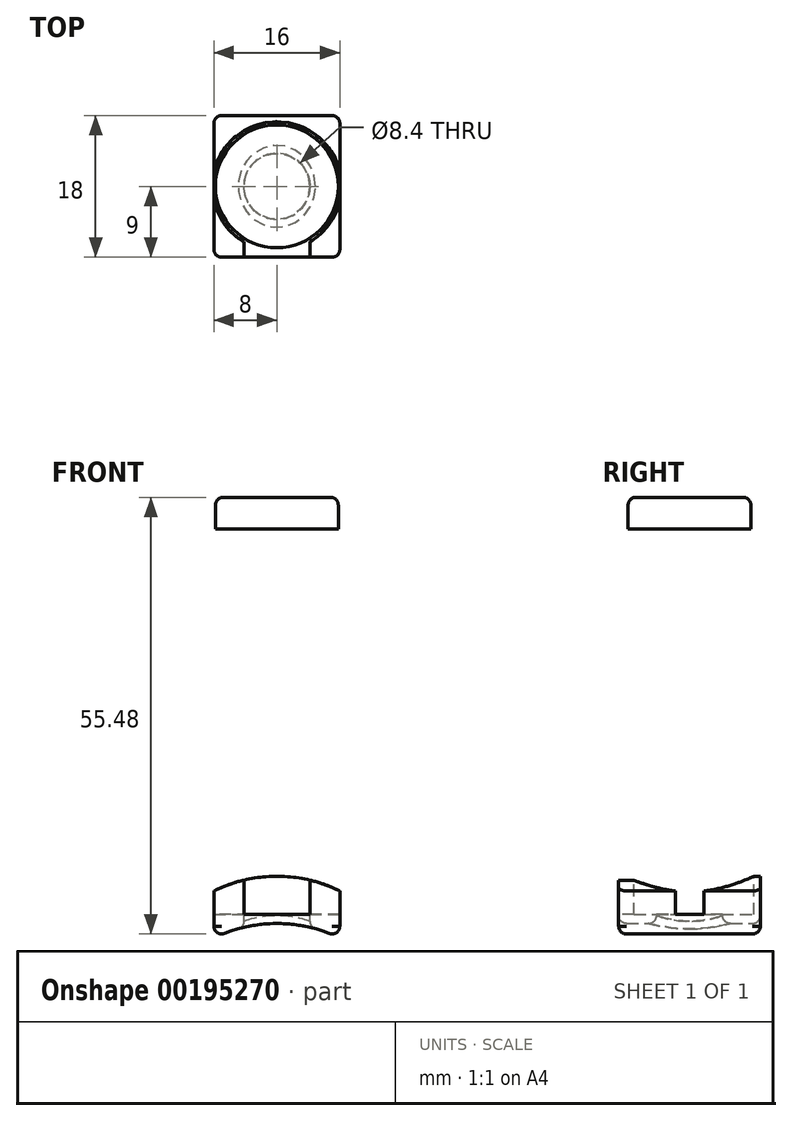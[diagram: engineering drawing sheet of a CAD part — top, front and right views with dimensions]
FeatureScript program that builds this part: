
annotation { "Feature Type Name" : "Feature", "Feature Type Description" : "" }
export const myFeature = defineFeature(function(context is Context, id is Id, definition is map)
    precondition{}
    {
        {
            var Q0;
            Q0=qCreatedBy(makeId("Front.planeOp"),FACE);
            var sketch = newSketch(context, id + "F0", { "sketchPlane" : qUnion([Q0])});
            skLineSegment(sketch, "E0.left", {"start": v(8, 2.02) * mm, "end": v(8, -2.02) * mm});
            skLineSegment(sketch, "E0.right", {"start": v(-8, 2.02) * mm, "end": v(-8, -2.02) * mm});
            skPoint(sketch, "E0.middle", {"position": v(0, 0) * mm});
            skArc(sketch, "E1", {"start": v(8, -2.02) * mm, "mid": v(0, -0.14) * mm, "end": v(-8, -2.02) * mm});
            skArc(sketch, "E2", {"start": v(8, 3.98) * mm, "mid": v(0, 5.86) * mm, "end": v(-8, 3.98) * mm});
            skLineSegment(sketch, "E3", {"start": v(-8, 2.02) * mm, "end": v(-8, 3.98) * mm});
            skLineSegment(sketch, "E4", {"start": v(8, 2.02) * mm, "end": v(8, 3.98) * mm});
            skSolve(sketch);
        }
        {
            var Q0;
            Q0=qSketchRegion(id+"F0",true);
            extrude(context, id + "F1", {"entities" : qUnion([Q0]), "endBound" : BoundingType.SYMMETRIC, "depth" : 18 * mm});
        }
        {
            var Q0;
            Q0=qCreatedBy(makeId("Top.planeOp"),FACE);
            cPlane(context, id + "F2", {"entities" : qUnion([Q0]), "cplaneType" : CPlaneType.OFFSET, "offset" : 25 * mm, "width" : 150 * mm, "height" : 150 * mm});
        }
        {
            var Q0;
            Q0=qCreatedBy(id+"F2.planeOp",FACE);
            var sketch = newSketch(context, id + "F3", { "sketchPlane" : qUnion([Q0])});
            skCircle(sketch, "E5", {"center": v(0, 0) * mm, "radius": 4.2 * mm});
            skArc(sketch, "E6", {"start": v(4.2, -7.04) * mm, "mid": v(0, 8.2) * mm, "end": v(-4.2, -7.04) * mm});
            skLineSegment(sketch, "E7.top", {"start": v(-4.2, -9) * mm, "end": v(4.2, -9) * mm});
            skLineSegment(sketch, "E7.left", {"start": v(-4.2, -7.04) * mm, "end": v(-4.2, -9) * mm});
            skLineSegment(sketch, "E7.right", {"start": v(4.2, -7.04) * mm, "end": v(4.2, -9) * mm});
            skSolve(sketch);
        }
        {
            var Q0;
            Q0=makeQuery(id+"F3.imprint","IMPRINT",FACE,{"disambiguationData":[TD([[makeQuery(id+"F3.imprint","IMPRINT",EDGE,{"derivedFrom":sQuery(id+"F3.wireOp",EDGE,"E5")}),1.0]])]});
            extrude(context, id + "F4", {"entities" : qUnion([Q0]), "operationType" : NewBodyOperationType.REMOVE, "endBound" : BoundingType.THROUGH_ALL, "oppositeDirection" : true, "depth" : 25 * mm});
        }
        {
            var Q0;
            Q0=makeQuery(id+"F3.imprint","IMPRINT",FACE,{"disambiguationData":[TD([[makeQuery(id+"F3.imprint","IMPRINT",EDGE,{"derivedFrom":sQuery(id+"F3.wireOp",EDGE,"E5")}),-1.0]])]});
            extrude(context, id + "F5", {"entities" : qUnion([Q0]), "operationType" : NewBodyOperationType.REMOVE, "oppositeDirection" : true, "depth" : 24 * mm});
        }
        {
            var Q0;
            Q0=qCreatedBy(id+"F2.planeOp",FACE);
            cPlane(context, id + "F6", {"entities" : qUnion([Q0]), "cplaneType" : CPlaneType.OFFSET, "offset" : 25 * mm, "width" : 150 * mm, "height" : 150 * mm});
        }
        {
            var Q0;
            Q0=qCreatedBy(id+"F6.planeOp",FACE);
            var sketch = newSketch(context, id + "F7", { "sketchPlane" : qUnion([Q0])});
            skCircle(sketch, "E8", {"center": v(0, 0) * mm, "radius": 7.8 * mm});
            skSolve(sketch);
        }
        {
            var Q0;
            Q0=makeQuery(id+"F7.imprint","IMPRINT",FACE,{"disambiguationData":[TD([[makeQuery(id+"F7.imprint","IMPRINT",EDGE,{"derivedFrom":sQuery(id+"F7.wireOp",EDGE,"E8")}),1.0]])]});
            extrude(context, id + "F8", {"entities" : qUnion([Q0]), "depth" : 4 * mm});
        }
        {
            var Q0;
            Q0=makeQuery(id+"F1.opExtrude","CAP_EDGE",EDGE,{"disambiguationData":[OSD([sQuery(id+"F0.wireOp",EDGE,"E0.left"),sQuery(id+"F0.wireOp",EDGE,"E4")])],"isStart":false});
            var Q1;
            Q1=makeQuery(id+"F1.opExtrude","CAP_EDGE",EDGE,{"disambiguationData":[OSD([sQuery(id+"F0.wireOp",EDGE,"E0.left"),sQuery(id+"F0.wireOp",EDGE,"E4")])],"isStart":true});
            var Q2;
            Q2=makeQuery(id+"F1.opExtrude","CAP_EDGE",EDGE,{"disambiguationData":[OSD([sQuery(id+"F0.wireOp",EDGE,"E0.right"),sQuery(id+"F0.wireOp",EDGE,"E3")])],"isStart":false});
            var Q3;
            Q3=makeQuery(id+"F1.opExtrude","CAP_EDGE",EDGE,{"disambiguationData":[OSD([sQuery(id+"F0.wireOp",EDGE,"E0.right"),sQuery(id+"F0.wireOp",EDGE,"E3")])],"isStart":true});
            var Q4;
            Q4=makeQuery(id+"F8.opExtrude","CAP_EDGE",EDGE,{"disambiguationData":[OSD([sQuery(id+"F7.wireOp",EDGE,"E8")])],"isStart":false});
            fillet(context, id + "F9", {"entities" : qUnion([Q0, Q1, Q2, Q3, Q4]), "radius" : 1 * mm, "tangentPropagation" : true, "allowEdgeOverflow" : false});
        }
        {
            var Q0;
            Q0=makeQuery(id+"F1.opExtrude","SWEPT_EDGE",EDGE,{"disambiguationData":[OSD([sQuery(id+"F0.wireOp",EDGE,"E0.right"),sQuery(id+"F0.wireOp",EDGE,"E1")])]});
            var Q1;
            Q1=makeQuery(id+"F4.boolean.opBoolean","INTERSECT",EDGE,{"derivedFrom":[makeQuery(id+"F1.opExtrude","SWEPT_FACE",FACE,{"disambiguationData":[OSD([sQuery(id+"F0.wireOp",EDGE,"E1")])]}),makeQuery(id+"F4.opExtrude","SWEPT_FACE",FACE,{"disambiguationData":[OSD([sQuery(id+"F3.wireOp",EDGE,"E5")])]})]});
            fillet(context, id + "F10", {"entities" : qUnion([Q0, Q1]), "radius" : 1 * mm, "tangentPropagation" : true, "allowEdgeOverflow" : false});
        }
    });
